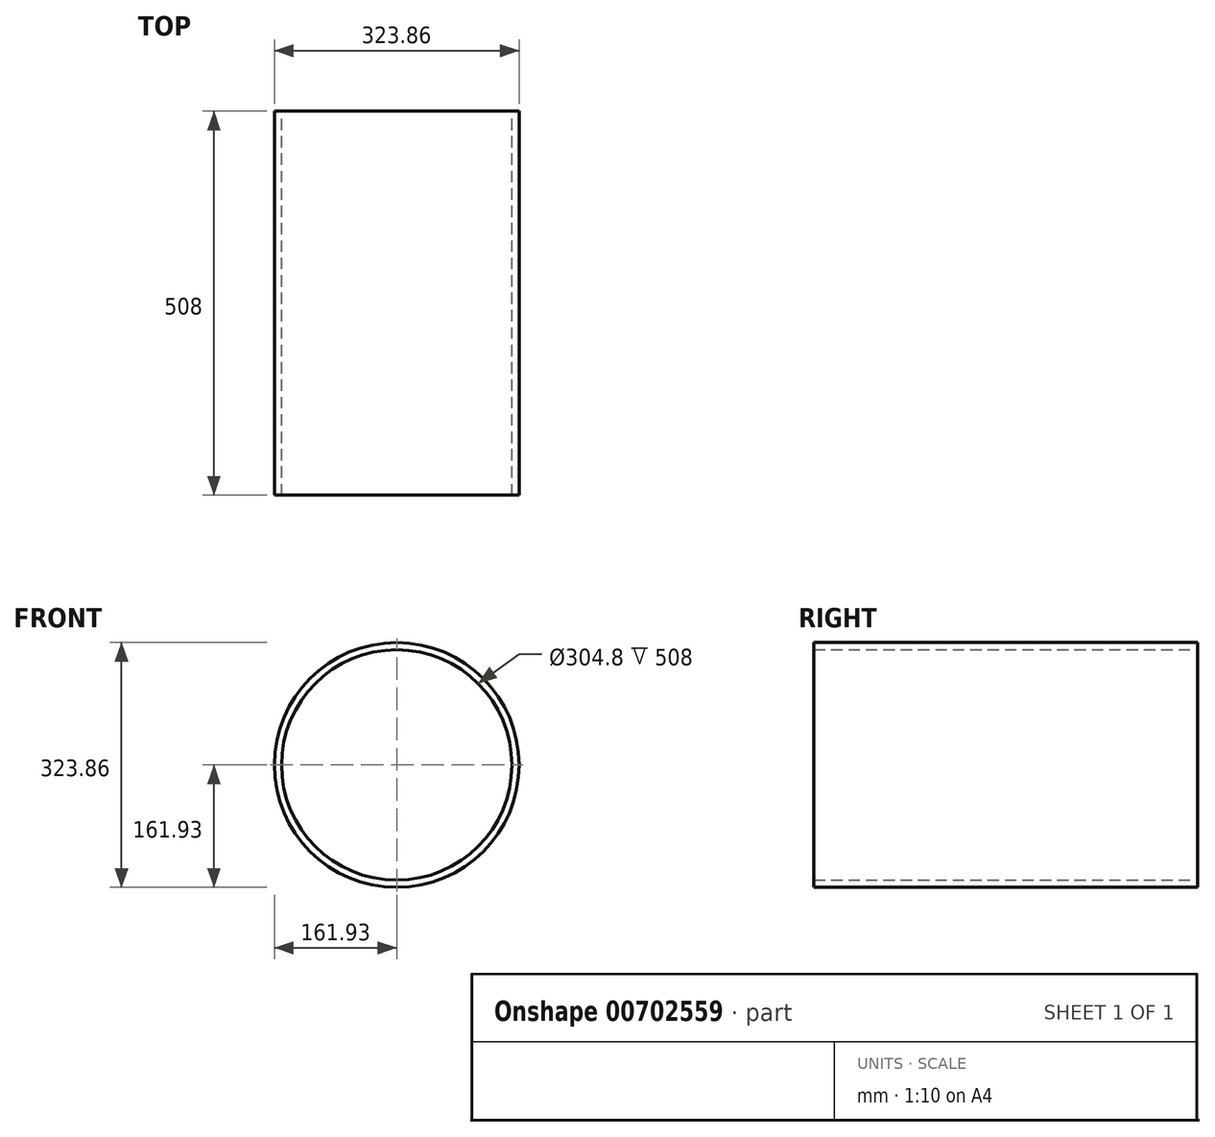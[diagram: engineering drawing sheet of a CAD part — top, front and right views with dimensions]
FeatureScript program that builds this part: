
annotation { "Feature Type Name" : "Feature", "Feature Type Description" : "" }
export const myFeature = defineFeature(function(context is Context, id is Id, definition is map)
    precondition{}
    {
        {
            var Q0;
            Q0=qCreatedBy(makeId("Front.planeOp"),FACE);
            var sketch = newSketch(context, id + "F0", { "sketchPlane" : qUnion([Q0])});
            skCircle(sketch, "E0", {"center": v(0, 0) * mm, "radius": 161.93 * mm});
            skCircle(sketch, "E1", {"center": v(0, 0) * mm, "radius": 152.4 * mm});
            skSolve(sketch);
        }
        {
            var Q0;
            Q0 = qSketchRegion(id + "F0", true);
            extrude(context, id + "F1", {"entities" : qUnion([Q0]), "endBound" : BoundingType.SYMMETRIC, "depth" : 508 * mm, "offsetDistance" : 25.4 * mm});
        }
    });
